# Revit family: A152400S-FG-W32
name_source: partatom
category: Plumbing Fixtures
revit_build: Autodesk Revit MEP 2016 (Build: 20150220_1215(x64)
units: mm (PartAtom-declared; Revit-internal decimal feet)

## family parameters
Cut with Voids When Loaded = No
Host = Face
OmniClass Number = 23.65.70.14.11
OmniClass Title = Drinking Fountains/Coolers
Part Type = Normal
Room Calculation Point = No
Round Connector Dimension = Use Diameter
Shared = Yes

## types (1)
- A152400S-FG-W32
    AP3 - Access Panel for a Dual Fountain  (Must Select -MF8) = No
    Assembly Code = D2010810
    CW Connection = Yes
    CWFU = 1.5
    Default Elevation = 34 15/16"
    Description = 14-Gage Stainless Steel Box Barrier-Free Wall Mount Bi-Level Drinking Fountain
    FRA4 - Freeze Resistant Valve System = No
    HW Connection = No
    HWFU = 0
    MF8 - Mounting Frame for a Dual Fountain = No
    Manufacturer = Murdock Manufacturing
    Material = 304 Stainless Steel
    Model = A152400S-FG-W32
    Product URL = https://www.murdockmfg.com
    RBL-  Reverse Bi-Level = No
    SK2- Skirt Kit, Stainless Steel for Upper Unit = No
    URL = https://www.murdockmfg.com
    Vent Connection = No
    W32-CSC - Concealed support Carrier = No
    WF1 - 1500 Gallon Capacity, NSF 42 + 53, 1 micron lead reduction filter = No
    WFU = 2
    Waste Connection = Yes

## geometry (parser evidence)
native form markers: Sweep x16
no freeform markers — native parametric forms only
